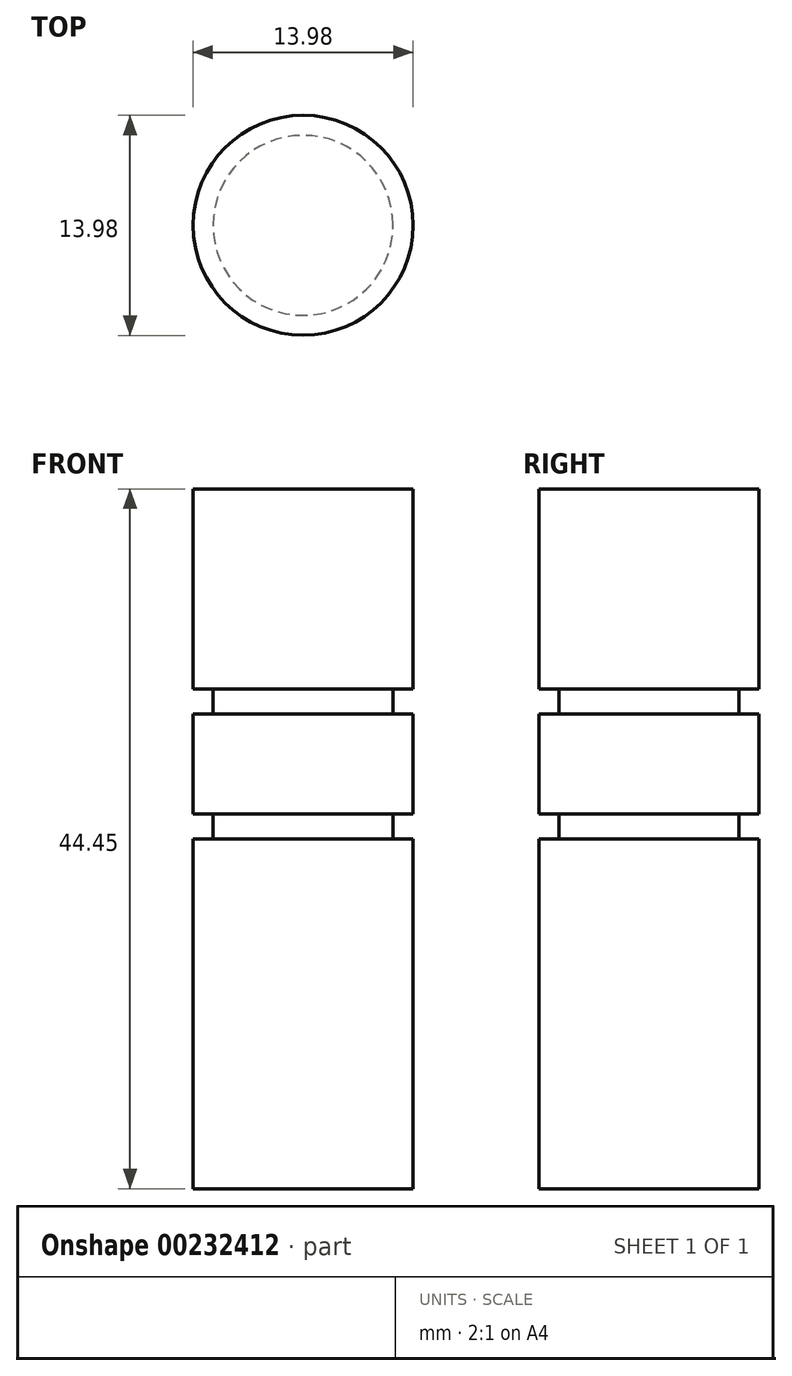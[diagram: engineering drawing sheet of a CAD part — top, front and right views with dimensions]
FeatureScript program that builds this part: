
annotation { "Feature Type Name" : "Feature", "Feature Type Description" : "" }
export const myFeature = defineFeature(function(context is Context, id is Id, definition is map)
    precondition{}
    {
        {
            var Q0;
            Q0=qCreatedBy(makeId("Right.planeOp"),FACE);
            var sketch = newSketch(context, id + "F0", { "sketchPlane" : qUnion([Q0])});
            skLineSegment(sketch, "E0.bottom", {"start": v(0, 0) * mm, "end": v(6.99, 0) * mm});
            skLineSegment(sketch, "E0.top", {"start": v(0, -44.45) * mm, "end": v(6.99, -44.45) * mm});
            skLineSegment(sketch, "E0.left", {"start": v(0, 0) * mm, "end": v(0, -44.45) * mm});
            skLineSegment(sketch, "E0.right", {"start": v(6.99, 0) * mm, "end": v(6.99, -12.7) * mm});
            skLineSegment(sketch, "E1", {"start": v(6.99, -12.7) * mm, "end": v(5.72, -12.7) * mm});
            skLineSegment(sketch, "E2", {"start": v(5.72, -12.7) * mm, "end": v(5.72, -14.29) * mm});
            skLineSegment(sketch, "E3", {"start": v(5.72, -14.29) * mm, "end": v(6.99, -14.29) * mm});
            skLineSegment(sketch, "E4", {"start": v(6.99, -14.29) * mm, "end": v(6.99, -20.64) * mm});
            skLineSegment(sketch, "E5", {"start": v(6.99, -20.64) * mm, "end": v(5.72, -20.64) * mm});
            skLineSegment(sketch, "E6", {"start": v(5.72, -20.64) * mm, "end": v(5.72, -22.23) * mm});
            skLineSegment(sketch, "E7", {"start": v(5.72, -22.23) * mm, "end": v(6.99, -22.23) * mm});
            skLineSegment(sketch, "E8.trimOffspring", {"start": v(6.99, -22.23) * mm, "end": v(6.99, -44.45) * mm});
            skSolve(sketch);
        }
        {
            var Q0;
            Q0=makeQuery(id+"F0.imprint","IMPRINT",FACE,{"disambiguationData":[TD([[makeQuery(id+"F0.imprint","IMPRINT",EDGE,{"derivedFrom":sQuery(id+"F0.wireOp",EDGE,"E0.bottom")}),-1.0]])]});
            var Q1;
            Q1=sQuery(id+"F0.wireOp",EDGE,"E0.left");
            revolve(context, id + "F1", {"entities" : qUnion([Q0]), "axis" : qUnion([Q1]), "revolveType" : RevolveType.FULL});
        }
    });
